# Revit family: Remeha_GasAce220-160_2Boiler-InLine_LOD5
name_source: partatom
category: Mechanical Equipment
revit_build: Autodesk Revit 2016 (Build: 20150714_1515(x64)
units: mm (PartAtom-declared; Revit-internal decimal feet)

## family parameters
Always vertical = Yes
Cut with Voids When Loaded = Yes
OmniClass Number = 23.75.10.11.14
OmniClass Title = Hot Water Heat Generators
Part Type = Normal
Room Calculation Point = No
Round Connector Dimension = Use Diameter
Shared = No
Work Plane-Based = No

## types (1)
- Gas Ace 220 - 2x160
    Access Clearance Bottom = 0.00 mm
    Access Clearance Front = 1100.00 mm
    Access Clearance Left = 500.00 mm
    Access Clearance Rear = 400.00 mm
    Access Clearance Right = 500.00 mm
    Access Clearance Top = 0.00 mm
    Additional Technical Details = https://www.remeha.co.uk
    Air Inlet Connection Size = 150.00 mm
    Annually = As Per Attached URL O&M Manual
    BMS Links = Yes
    Building Regulations Seasonal Efficiency = 95.90
    Burner Control Type = Modulating
    CE Mark = Yes
    Colour = RAL 2002 (vermillion)
    Condensate Drain Size = 40.00 mm
    Condensate Drain Type = Plain
    Configuration = Cascade boilers
    Control Type = 0 - 10V, Open Therm, Volt free enable, Direct boiler weather compensating control systems available from Remeha as optional extra's.
    Drain Connection Size = 20.00 mm
    Drain Connection Type = Threaded
    Energy Technology List = https://etl.beis.gov.uk
    ErP Energy Label = 0
    ErP Rated Efficiency at Full Load = 87.8
    ErP Rated Efficiency at Part Load = 97.8
    ErP Seasonal Efficiency = 0
    Expected Life = 15
    External Material = Steel
    Features = Remeha's Gas 220 Ace Cascade systems are compact high efficiency condensing boilers. Lighter and more efficienct, their size make them ideally suited to modular arrangments
    Finish = High PolishGardner 60 Grad 91EH
    Flow and Return Connection Size = 125.00 mm
    Flow and Return Connection Type = Flanged
    Flue Connection size = 150.00 mm
    Flue or Air Intake Classification = B23p
    Frequency = 50 Hz
    Fuel Connection Size = 65.00 mm
    Fuel Connection Type = Flanged
    Full Load Current = 0 A
    Fuse Rating = 6 A
    Gas Consumption rate = 33.0
    Gross Weight = 1019.00 kg
    Heat Exchanger Material = Aluminium
    Heater Operation = Condensing
    Hydraulic Resistance at 11C temperature differential = 0.00000
    Hydraulic Resistance at 20C temperature differential = 0.19000
    IP Rating = IPX1B
    IfcExportAs = IfcBoilerType
    IfcExportType = NOTDEFINED
    Interlocks = Yes
    Load Classification = Power
    Manufacturer = Remeha
    Manufacturer Website = www.remeha.co.uk
    Maximum Gas Inlet Pressure = 0.02500 bar
    Maximum Oil Inlet Pressure = 0.00000 bar
    Maximum Operating Pressure = 5.00000 bar
    Maximum Power Consumption = 275 W
    Minimum Flow Rate at 11C temperature differential = 0.0 L/s
    Minimum Flow Rate at 20C temperature differential = 1.8 L/s
    Minimum Gas Inlet Pressure = 0.01700 bar
    Minimum Oil Inlet Pressure = 0.00000 bar
    Minimum Operating Pressure = 0.80000 bar
    Minimum Power Consumption = 5 W
    Mounting = Floor Standing
    NOx Emissions = 36
    Nominal Gas Inlet Pressure = 0.02000 bar
    Nominal Oil Inlet Pressure = 0.00000 bar
    Oil Consumption rate = 0
    Operation and Maintenance Manual = https://www.remeha.co.uk
    Optional Fuel = Gas - LPG
    Overall Height = 2282.00 mm
    Overall Length = 3145.00 mm
    Overall Width = 874.00 mm
    Primary Fuel = Gas - NG
    Product Literature = https://www.remeha.co.uk
    Product Model Number = KTSGA2L
    Product Range = Gas 220 Ace 2 x In Line cascade 160
    Rated Criteria = 80/60
    Rated Output = 304200 W
    Reference Standard = 2009/142/EC : 92/42/EEC
    Safety Valve Connection Size = 0.00 mm
    Safety Valve Connection Type = Threaded
    Shape = Rectangular (Vertical)
    Shipping Weight = 0.00 kg
    Sound Pressure Level = 58.7
    Starting Current = 0 A
    Supply Phase = 1
    Turndown Ratio = 4.8
    Type = Space heating
    Voltage = 230 V
    Water Content = 178.0 L
    Water Treatment Required = Yes

note: source unit labels omitted for Hydraulic Resistance at 11C temperature differential, Hydraulic Resistance at 20C temperature differential — the stored unit's dimension contradicts the parameter name (converter mislabeling)

## geometry (parser evidence)
native form markers: Sweep x26
no freeform markers — native parametric forms only
